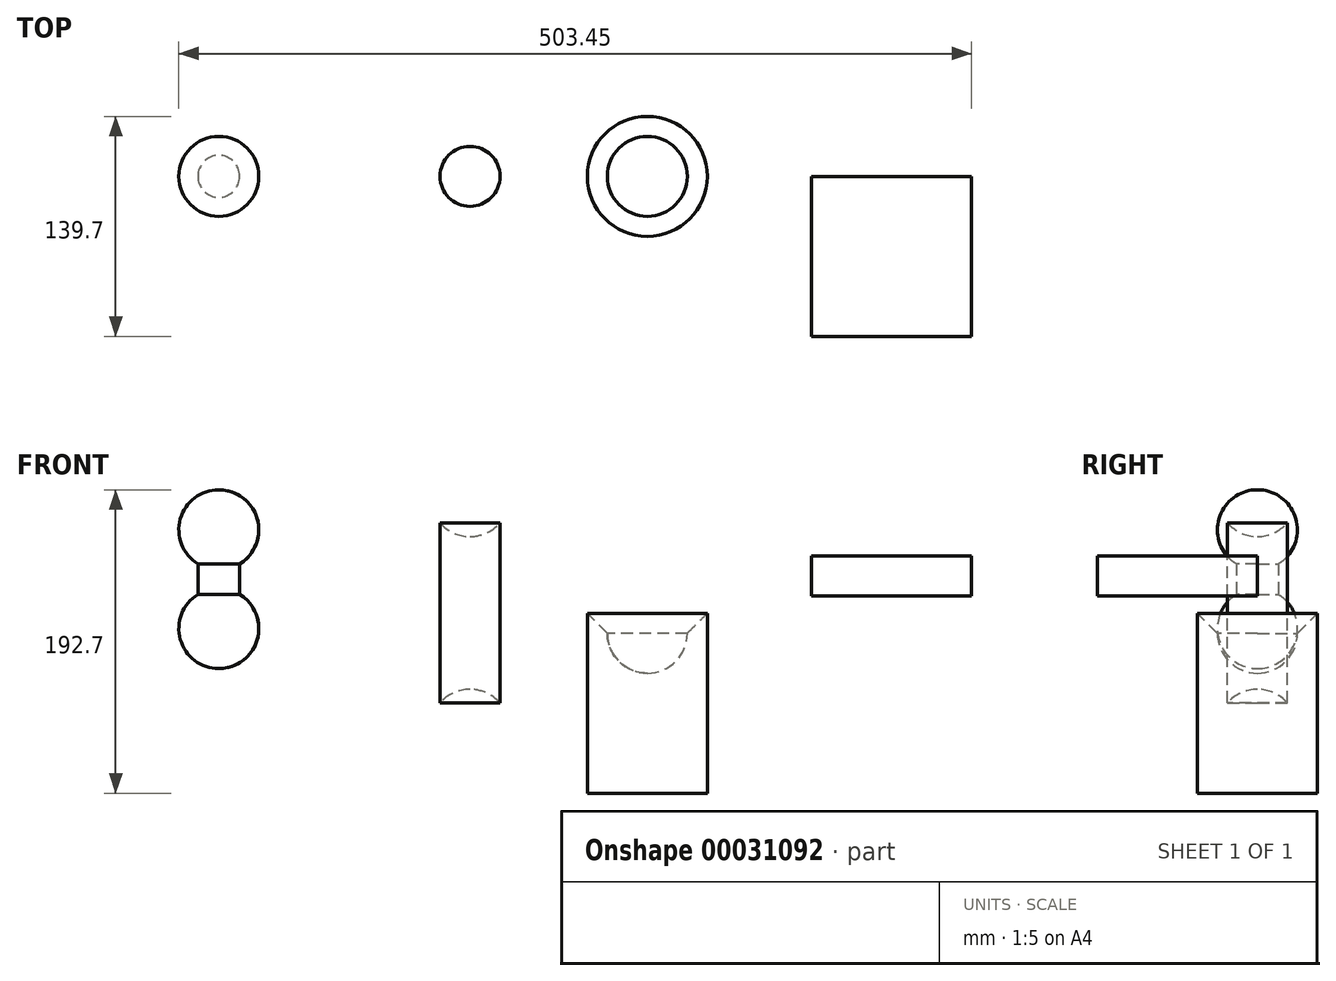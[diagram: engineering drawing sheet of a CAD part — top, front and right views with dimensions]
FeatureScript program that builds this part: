
annotation { "Feature Type Name" : "Feature", "Feature Type Description" : "" }
export const myFeature = defineFeature(function(context is Context, id is Id, definition is map)
    precondition{}
    {
        {
            var Q0;
            Q0=qCreatedBy(makeId("Front.planeOp"),FACE);
            var sketch = newSketch(context, id + "F0", { "sketchPlane" : qUnion([Q0])});
            skLineSegment(sketch, "E0.bottom", {"start": v(-41.92, -48.38) * mm, "end": v(59.68, -48.38) * mm});
            skLineSegment(sketch, "E0.top", {"start": v(-41.92, -22.98) * mm, "end": v(59.68, -22.98) * mm});
            skLineSegment(sketch, "E0.left", {"start": v(-41.92, -48.38) * mm, "end": v(-41.92, -22.98) * mm});
            skLineSegment(sketch, "E0.right", {"start": v(59.68, -48.38) * mm, "end": v(59.68, -22.98) * mm});
            skSolve(sketch);
        }
        {
            var Q0;
            Q0 = qSketchRegion(id + "F0", true);
            extrude(context, id + "F1", {"entities" : qUnion([Q0]), "depth" : 101.6 * mm});
        }
        {
            var Q0;
            Q0=qCreatedBy(makeId("Front.planeOp"),FACE);
            var sketch = newSketch(context, id + "F2", { "sketchPlane" : qUnion([Q0])});
            skLineSegment(sketch, "E1", {"start": v(-258.83, -4.12) * mm, "end": v(-258.83, -67.62) * mm});
            skLineSegment(sketch, "E2.left", {"start": v(-258.83, -10.47) * mm, "end": v(-258.83, -107.57) * mm});
            skLineSegment(sketch, "E2.right", {"start": v(-239.78, -1.87) * mm, "end": v(-239.78, -116.17) * mm});
            skArc(sketch, "E3", {"start": v(-239.78, -116.17) * mm, "mid": v(-248.38, -109.82) * mm, "end": v(-258.83, -107.57) * mm});
            skArc(sketch, "E4", {"start": v(-258.83, -10.47) * mm, "mid": v(-248.38, -8.22) * mm, "end": v(-239.78, -1.87) * mm});
            skPoint(sketch, "E5.orphan", {"position": v(-239.78, -132.97) * mm});
            skSolve(sketch);
        }
        {
            var Q0;
            Q0=makeQuery(id+"F2.imprint","IMPRINT",FACE,{"disambiguationData":[TD([[makeQuery(id+"F2.imprint","IMPRINT",EDGE,{"derivedFrom":sQuery(id+"F2.wireOp",EDGE,"E2.left")}),1.0]])]});
            var Q1;
            Q1=sQuery(id+"F2.wireOp",EDGE,"E1");
            revolve(context, id + "F3", {"entities" : qUnion([Q0]), "axis" : qUnion([Q1]), "revolveType" : RevolveType.FULL});
        }
        {
            var Q0;
            Q0=qCreatedBy(makeId("Front.planeOp"),FACE);
            var sketch = newSketch(context, id + "F4", { "sketchPlane" : qUnion([Q0])});
            skArc(sketch, "E6", {"start": v(-418.37, -94.36) * mm, "mid": v(-393.93, -75.88) * mm, "end": v(-405.05, -47.33) * mm});
            skLineSegment(sketch, "E7", {"start": v(-418.37, -99.76) * mm, "end": v(-418.37, 19.2) * mm, "construction": true});
            skLineSegment(sketch, "E8", {"start": v(-405.05, -47.33) * mm, "end": v(-405.05, -27.83) * mm});
            skArc(sketch, "E9", {"start": v(-405.05, -27.83) * mm, "mid": v(-393.93, 0.72) * mm, "end": v(-418.37, 19.2) * mm});
            skPoint(sketch, "E10.orphan", {"position": v(-405.05, -6.2) * mm});
            skLineSegment(sketch, "E11", {"start": v(-418.37, 19.2) * mm, "end": v(-418.37, -94.36) * mm});
            skSolve(sketch);
        }
        {
            var Q0;
            Q0 = qSketchRegion(id + "F4", true);
            var Q1;
            Q1=sQuery(id+"F4.wireOp",EDGE,"E7");
            revolve(context, id + "F5", {"entities" : qUnion([Q0]), "axis" : qUnion([Q1]), "revolveType" : RevolveType.FULL});
        }
        {
            var Q0;
            Q0=qCreatedBy(makeId("Front.planeOp"),FACE);
            var sketch = newSketch(context, id + "F6", { "sketchPlane" : qUnion([Q0])});
            skLineSegment(sketch, "E12", {"start": v(-146.2, -99.32) * mm, "end": v(-146.2, -183.14) * mm, "construction": true});
            skLineSegment(sketch, "E13.top", {"start": v(-146.2, -173.5) * mm, "end": v(-120.8, -173.5) * mm});
            skLineSegment(sketch, "E13.left", {"start": v(-146.2, -97.3) * mm, "end": v(-146.2, -173.5) * mm, "construction": true});
            skLineSegment(sketch, "E14", {"start": v(-146.2, -97.3) * mm, "end": v(-146.2, -173.5) * mm});
            skPoint(sketch, "E15.orphan", {"position": v(-120.8, -71.9) * mm});
            skArc(sketch, "E16", {"start": v(-146.2, -97.3) * mm, "mid": v(-128.23, -89.86) * mm, "end": v(-120.8, -71.9) * mm});
            skLineSegment(sketch, "E17", {"start": v(-146.2, -173.5) * mm, "end": v(-108.1, -173.5) * mm});
            skPoint(sketch, "E17.endSnap0", {"position": v(-133.5, -173.5) * mm});
            skPoint(sketch, "E18.start.orphan", {"position": v(-128.23, -71.9) * mm});
            skLineSegment(sketch, "E19", {"start": v(-108.1, -69.41) * mm, "end": v(-108.1, -173.5) * mm});
            skLineSegment(sketch, "E20", {"start": v(-120.8, -71.9) * mm, "end": v(-108.1, -59.2) * mm});
            skLineSegment(sketch, "E21", {"start": v(-108.1, -59.2) * mm, "end": v(-108.1, -69.41) * mm});
            skSolve(sketch);
        }
        {
            var Q0;
            {var subQ2=sQuery(id+"F6.wireOp",EDGE,"E14");Q0=makeQuery(id+"F6.imprint","IMPRINT",FACE,{"disambiguationData":[TD([[makeQuery(id+"F6.imprint","IMPRINT",EDGE,{"derivedFrom":subQ2}),1.0]])]});}
            var Q1;
            Q1=sQuery(id+"F6.wireOp",EDGE,"E12");
            revolve(context, id + "F7", {"entities" : qUnion([Q0]), "axis" : qUnion([Q1]), "revolveType" : RevolveType.FULL});
        }
    });
